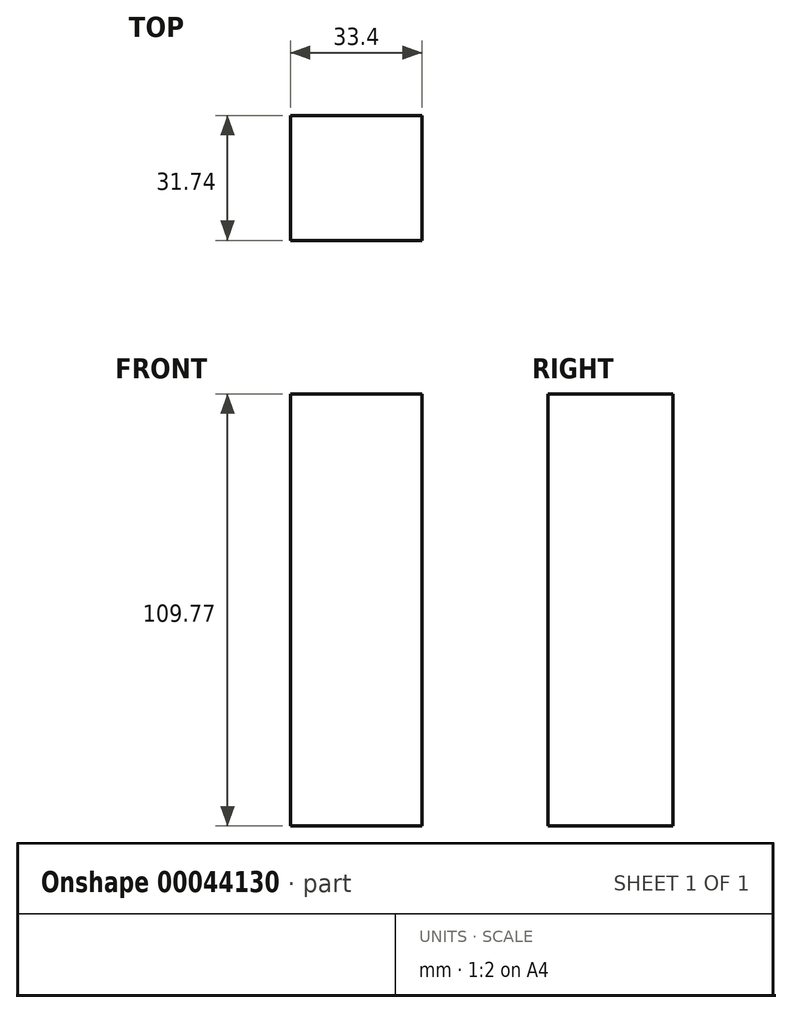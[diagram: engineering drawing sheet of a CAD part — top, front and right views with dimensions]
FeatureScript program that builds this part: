
annotation { "Feature Type Name" : "Feature", "Feature Type Description" : "" }
export const myFeature = defineFeature(function(context is Context, id is Id, definition is map)
    precondition{}
    {
        {
            var Q0;
            Q0=qCreatedBy(makeId("Top.planeOp"),FACE);
            var sketch = newSketch(context, id + "F0", { "sketchPlane" : qUnion([Q0])});
            skLineSegment(sketch, "E0.bottom", {"start": v(0, 0) * mm, "end": v(33.4, 0) * mm});
            skLineSegment(sketch, "E0.top", {"start": v(0, -31.74) * mm, "end": v(33.4, -31.74) * mm});
            skLineSegment(sketch, "E0.left", {"start": v(0, 0) * mm, "end": v(0, -31.74) * mm});
            skLineSegment(sketch, "E0.right", {"start": v(33.4, 0) * mm, "end": v(33.4, -31.74) * mm});
            skSolve(sketch);
        }
        {
            var Q0;
            Q0=makeQuery(id+"F0.imprint","IMPRINT",FACE,{"disambiguationData":[TD([[makeQuery(id+"F0.imprint","IMPRINT",EDGE,{"derivedFrom":sQuery(id+"F0.wireOp",EDGE,"E0.bottom")}),-1.0]])]});
            extrude(context, id + "F1", {"entities" : qUnion([Q0]), "depth" : 109.77 * mm});
        }
    });
